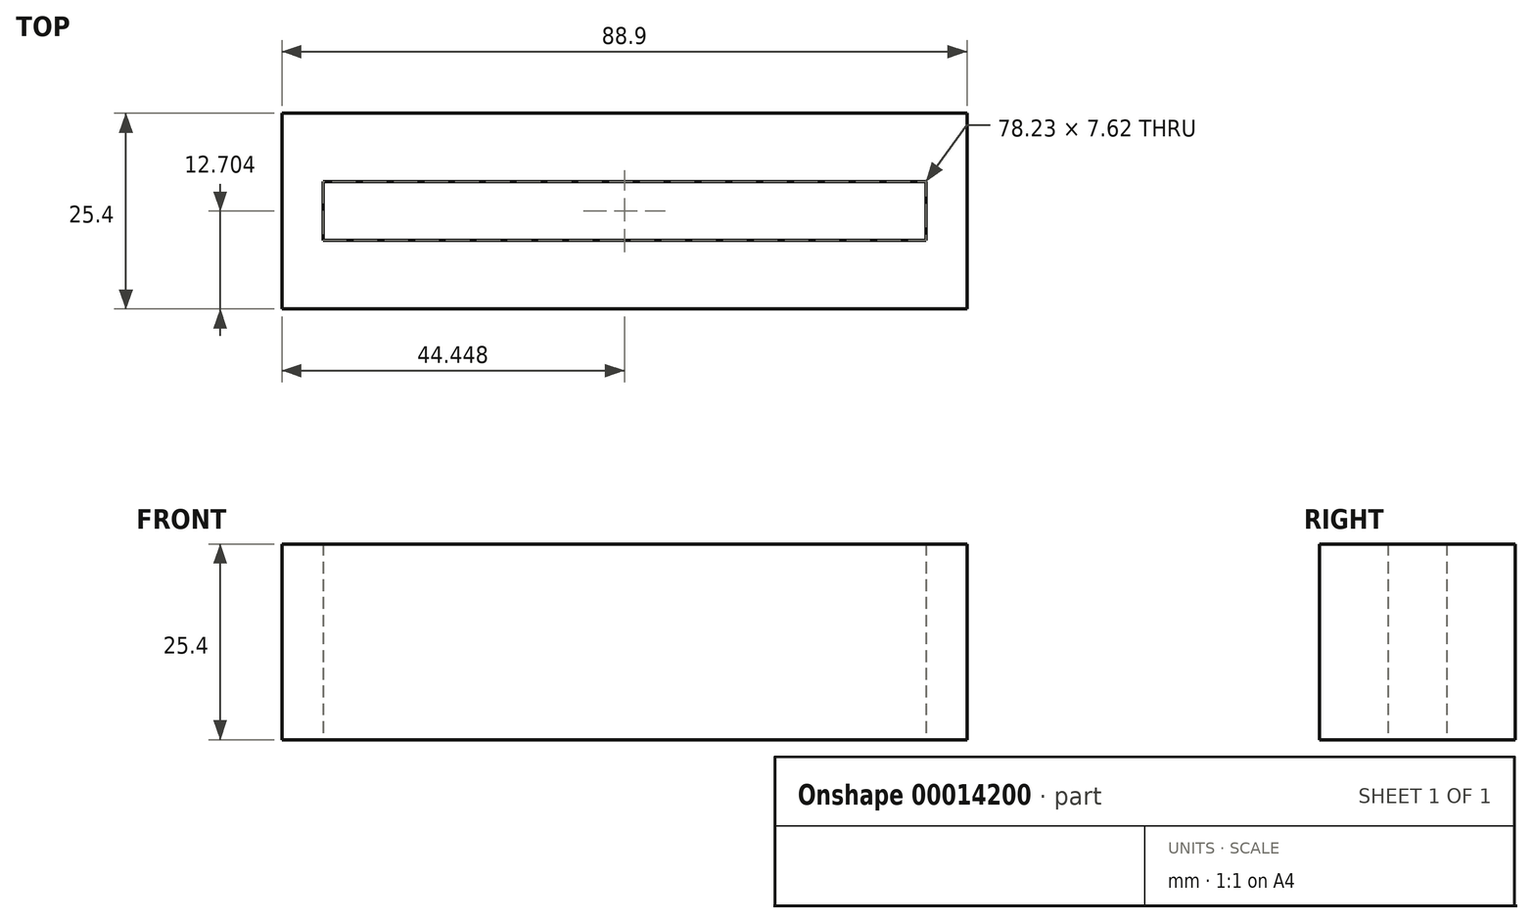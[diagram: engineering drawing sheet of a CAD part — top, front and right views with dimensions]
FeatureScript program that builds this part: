
annotation { "Feature Type Name" : "Feature", "Feature Type Description" : "" }
export const myFeature = defineFeature(function(context is Context, id is Id, definition is map)
    precondition{}
    {
        {
            var Q0;
            Q0=qCreatedBy(makeId("Top.planeOp"),FACE);
            var sketch = newSketch(context, id + "F0", { "sketchPlane" : qUnion([Q0])});
            skLineSegment(sketch, "E0.bottom", {"start": v(45.4, 2.76) * mm, "end": v(-43.5, 2.76) * mm});
            skLineSegment(sketch, "E0.top", {"start": v(45.4, -22.64) * mm, "end": v(-43.5, -22.64) * mm});
            skLineSegment(sketch, "E0.left", {"start": v(45.4, 2.76) * mm, "end": v(45.4, -22.64) * mm});
            skLineSegment(sketch, "E0.right", {"start": v(-43.5, 2.76) * mm, "end": v(-43.5, -22.64) * mm});
            skLineSegment(sketch, "E1.bottom", {"start": v(40.06, -6.13) * mm, "end": v(-38.17, -6.13) * mm});
            skLineSegment(sketch, "E1.top", {"start": v(40.06, -13.75) * mm, "end": v(-38.17, -13.75) * mm});
            skLineSegment(sketch, "E1.left", {"start": v(40.06, -6.13) * mm, "end": v(40.06, -13.75) * mm});
            skLineSegment(sketch, "E1.right", {"start": v(-38.17, -6.13) * mm, "end": v(-38.17, -13.75) * mm});
            skSolve(sketch);
        }
        {
            var Q0;
            Q0=makeQuery(id+"F0.imprint","IMPRINT",FACE,{"disambiguationData":[TD([[makeQuery(id+"F0.imprint","IMPRINT",EDGE,{"derivedFrom":sQuery(id+"F0.wireOp",EDGE,"E0.bottom")}),1.0]])]});
            extrude(context, id + "F1", {"entities" : qUnion([Q0]), "depth" : 25.4 * mm});
        }
    });
